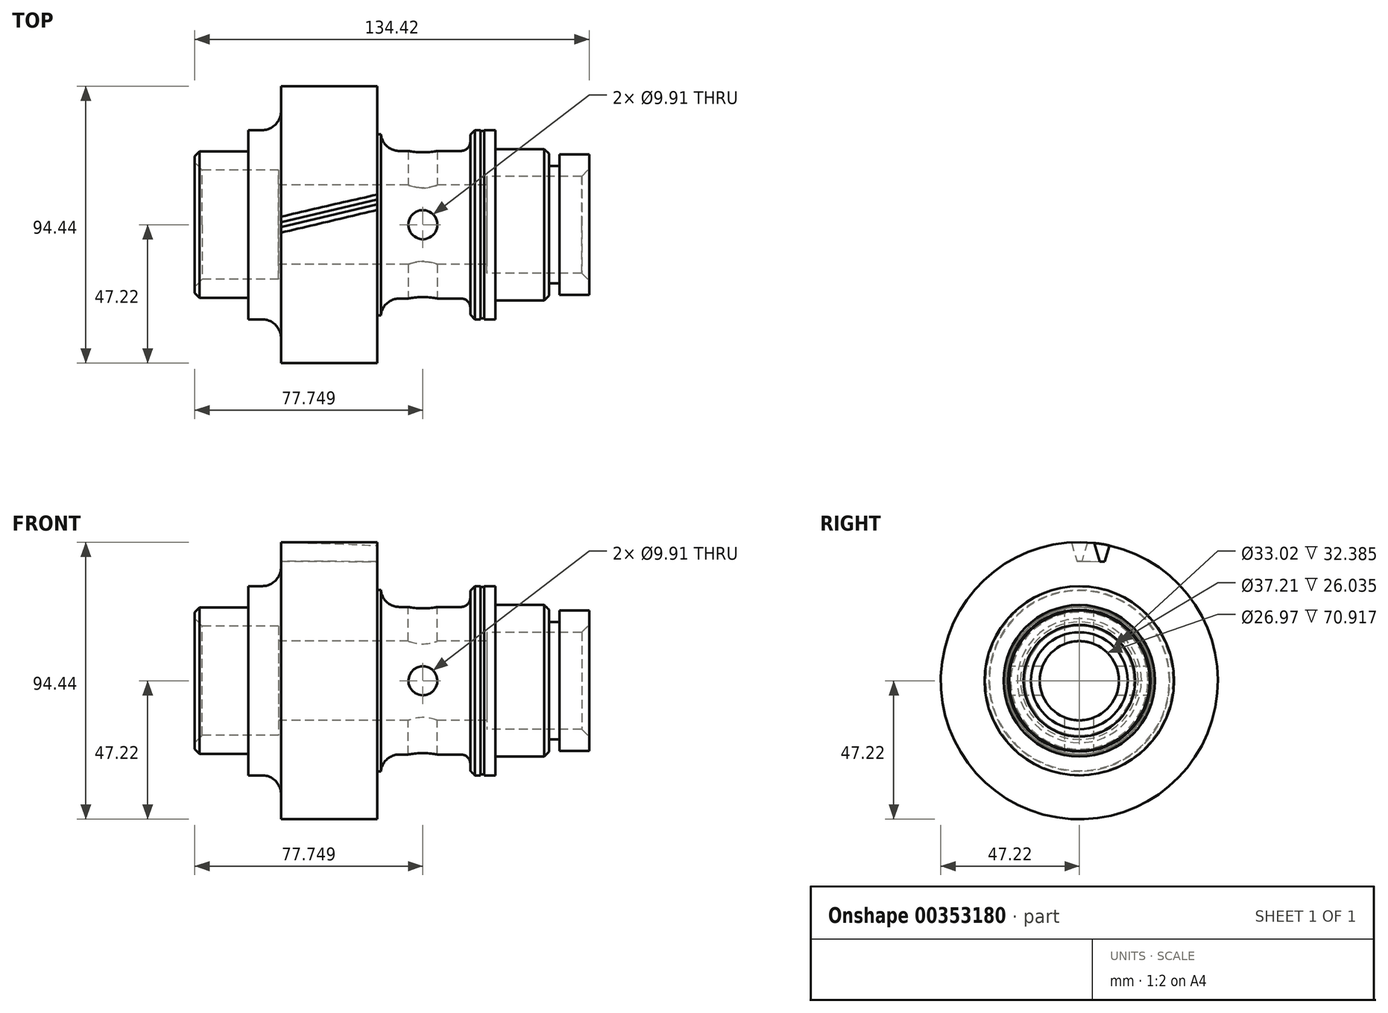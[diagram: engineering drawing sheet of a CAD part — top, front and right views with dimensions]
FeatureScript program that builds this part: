
annotation { "Feature Type Name" : "Feature", "Feature Type Description" : "" }
export const myFeature = defineFeature(function(context is Context, id is Id, definition is map)
    precondition{}
    {
        {
            var Q0;
            Q0=qCreatedBy(makeId("Front.planeOp"),FACE);
            var sketch = newSketch(context, id + "F0", { "sketchPlane" : qUnion([Q0])});
            skLineSegment(sketch, "E0", {"start": v(0, 0) * mm, "end": v(134.42, 0) * mm});
            skLineSegment(sketch, "E1", {"start": v(134.42, 0) * mm, "end": v(134.42, 23.94) * mm});
            skLineSegment(sketch, "E2", {"start": v(134.42, 23.94) * mm, "end": v(124.26, 23.94) * mm});
            skLineSegment(sketch, "E3", {"start": v(124.26, 23.94) * mm, "end": v(124.26, 20.02) * mm});
            skLineSegment(sketch, "E4", {"start": v(124.26, 20.02) * mm, "end": v(120.7, 20.02) * mm});
            skLineSegment(sketch, "E5", {"start": v(120.7, 20.02) * mm, "end": v(120.7, 25.8) * mm});
            skLineSegment(sketch, "E6", {"start": v(120.7, 25.8) * mm, "end": v(102.41, 25.8) * mm});
            skLineSegment(sketch, "E7", {"start": v(102.41, 25.8) * mm, "end": v(102.41, 32.26) * mm});
            skLineSegment(sketch, "E8", {"start": v(102.41, 32.26) * mm, "end": v(98.6, 32.26) * mm});
            skLineSegment(sketch, "E9", {"start": v(98.6, 32.26) * mm, "end": v(98.6, 31.94) * mm});
            skLineSegment(sketch, "E10", {"start": v(98.6, 31.94) * mm, "end": v(97.33, 31.94) * mm});
            skLineSegment(sketch, "E11", {"start": v(97.33, 31.94) * mm, "end": v(97.33, 32.26) * mm});
            skLineSegment(sketch, "E12", {"start": v(97.33, 32.26) * mm, "end": v(93.9, 32.26) * mm});
            skLineSegment(sketch, "E13", {"start": v(93.9, 32.26) * mm, "end": v(93.9, 25.15) * mm});
            skLineSegment(sketch, "E14", {"start": v(93.9, 25.15) * mm, "end": v(63.42, 25.15) * mm});
            skLineSegment(sketch, "E15", {"start": v(62.15, 47.22) * mm, "end": v(29.39, 47.22) * mm});
            skLineSegment(sketch, "E16", {"start": v(29.39, 47.22) * mm, "end": v(29.39, 32.26) * mm});
            skLineSegment(sketch, "E17", {"start": v(29.39, 32.26) * mm, "end": v(18.29, 32.26) * mm});
            skLineSegment(sketch, "E18", {"start": v(18.29, 24.92) * mm, "end": v(0, 24.92) * mm});
            skLineSegment(sketch, "E19", {"start": v(0, 24.92) * mm, "end": v(0, 0) * mm});
            skLineSegment(sketch, "E20", {"start": v(63.42, 25.15) * mm, "end": v(63.42, 30.87) * mm});
            skLineSegment(sketch, "E21", {"start": v(63.42, 30.87) * mm, "end": v(62.15, 30.87) * mm});
            skLineSegment(sketch, "E22", {"start": v(62.15, 30.87) * mm, "end": v(62.15, 47.22) * mm});
            skLineSegment(sketch, "E23", {"start": v(18.29, 24.92) * mm, "end": v(18.29, 32.26) * mm});
            skPoint(sketch, "E24.orphan", {"position": v(9.8, 32.26) * mm});
            skLineSegment(sketch, "E25", {"start": v(0, 18.6) * mm, "end": v(28.57, 18.6) * mm});
            skLineSegment(sketch, "E26", {"start": v(28.58, 18.6) * mm, "end": v(28.58, 13.49) * mm});
            skLineSegment(sketch, "E27", {"start": v(28.58, 13.49) * mm, "end": v(99.5, 13.49) * mm});
            skLineSegment(sketch, "E28", {"start": v(99.5, 13.49) * mm, "end": v(99.5, 16.51) * mm});
            skLineSegment(sketch, "E29", {"start": v(99.5, 16.51) * mm, "end": v(134.42, 16.51) * mm});
            skSolve(sketch);
        }
        {
            var Q0;
            {var subQ3=sQuery(id+"F0.wireOp",EDGE,"E2");Q0=makeQuery(id+"F0.imprint","IMPRINT",FACE,{"disambiguationData":[TD([[makeQuery(id+"F0.imprint","IMPRINT",EDGE,{"derivedFrom":subQ3}),1.0]])]});}
            var Q1;
            Q1=sQuery(id+"F0.wireOp",EDGE,"E0");
            revolve(context, id + "F1", {"entities" : qUnion([Q0]), "axis" : qUnion([Q1]), "revolveType" : RevolveType.FULL});
        }
        {
            var Q0;
            Q0=makeQuery(id+"F1.opRevolve","SWEPT_EDGE",EDGE,{"disambiguationData":[OSD([sQuery(id+"F0.wireOp",EDGE,"E14"),sQuery(id+"F0.wireOp",EDGE,"E20")])]});
            var Q1;
            Q1=makeQuery(id+"F1.opRevolve","SWEPT_EDGE",EDGE,{"disambiguationData":[OSD([sQuery(id+"F0.wireOp",EDGE,"E16"),sQuery(id+"F0.wireOp",EDGE,"E17")])]});
            fillet(context, id + "F2", {"entities" : qUnion([Q0, Q1]), "radius" : 6.35 * mm, "tangentPropagation" : true, "allowEdgeOverflow" : false});
        }
        {
            var Q0;
            Q0=makeQuery(id+"F1.opRevolve","SWEPT_EDGE",EDGE,{"disambiguationData":[OSD([sQuery(id+"F0.wireOp",EDGE,"E13"),sQuery(id+"F0.wireOp",EDGE,"E14")])]});
            fillet(context, id + "F3", {"entities" : qUnion([Q0]), "radius" : 3.17 * mm, "tangentPropagation" : true, "allowEdgeOverflow" : false});
        }
        {
            var Q0;
            Q0=makeQuery(id+"F1.opRevolve","SWEPT_EDGE",EDGE,{"disambiguationData":[OSD([sQuery(id+"F0.wireOp",EDGE,"E12"),sQuery(id+"F0.wireOp",EDGE,"E13")])]});
            var Q1;
            Q1=makeQuery(id+"F1.opRevolve","SWEPT_EDGE",EDGE,{"disambiguationData":[OSD([sQuery(id+"F0.wireOp",EDGE,"E5"),sQuery(id+"F0.wireOp",EDGE,"E6")])]});
            var Q2;
            Q2=makeQuery(id+"F1.opRevolve","SWEPT_EDGE",EDGE,{"disambiguationData":[OSD([sQuery(id+"F0.wireOp",EDGE,"E18"),sQuery(id+"F0.wireOp",EDGE,"E19")])]});
            chamfer(context, id + "F4", {"entities" : qUnion([Q0, Q1, Q2]), "width" : 1.57 * mm, "tangentPropagation" : true});
        }
        {
            var Q0;
            Q0=makeQuery(id+"F1.opRevolve","SWEPT_EDGE",EDGE,{"disambiguationData":[OSD([sQuery(id+"F0.wireOp",EDGE,"E19"),sQuery(id+"F0.wireOp",EDGE,"E25")])]});
            var Q1;
            Q1=makeQuery(id+"F1.opRevolve","SWEPT_EDGE",EDGE,{"disambiguationData":[OSD([sQuery(id+"F0.wireOp",EDGE,"E1"),sQuery(id+"F0.wireOp",EDGE,"E29")])]});
            chamfer(context, id + "F5", {"entities" : qUnion([Q0, Q1]), "width" : 2.54 * mm, "tangentPropagation" : true});
        }
        {
            var Q0;
            Q0=qCreatedBy(makeId("Top.planeOp"),FACE);
            var sketch = newSketch(context, id + "F6", { "sketchPlane" : qUnion([Q0])});
            skCircle(sketch, "E30", {"center": v(77.75, 0) * mm, "radius": 4.95 * mm});
            skSolve(sketch);
        }
        {
            var Q0;
            Q0=makeQuery(id+"F6.imprint","IMPRINT",FACE,{"disambiguationData":[TD([[makeQuery(id+"F6.imprint","IMPRINT",EDGE,{"derivedFrom":sQuery(id+"F6.wireOp",EDGE,"E30")}),1.0]])]});
            extrude(context, id + "F7", {"entities" : qUnion([Q0]), "operationType" : NewBodyOperationType.REMOVE, "endBound" : BoundingType.THROUGH_ALL, "oppositeDirection" : true, "depth" : 25.4 * mm, "hasSecondDirection" : true, "secondDirectionBound" : SecondDirectionBoundingType.THROUGH_ALL, "secondDirectionOppositeDirection" : false, "secondDirectionDepth" : 25.4 * mm});
        }
        {
            var Q0;
            Q0=qCreatedBy(makeId("Front.planeOp"),FACE);
            var sketch = newSketch(context, id + "F8", { "sketchPlane" : qUnion([Q0])});
            skCircle(sketch, "E31", {"center": v(77.75, 0) * mm, "radius": 4.95 * mm});
            skSolve(sketch);
        }
        {
            var Q0;
            Q0 = qSketchRegion(id + "F8", true);
            extrude(context, id + "F9", {"entities" : qUnion([Q0]), "operationType" : NewBodyOperationType.REMOVE, "endBound" : BoundingType.THROUGH_ALL, "oppositeDirection" : true, "depth" : 25.4 * mm, "hasSecondDirection" : true, "secondDirectionBound" : SecondDirectionBoundingType.THROUGH_ALL, "secondDirectionOppositeDirection" : false, "secondDirectionDepth" : 25.4 * mm});
        }
        {
            var Q0;
            Q0=makeQuery(id+"F1.opRevolve","SWEPT_FACE",FACE,{"disambiguationData":[OSD([sQuery(id+"F0.wireOp",EDGE,"E16")])]});
            var sketch = newSketch(context, id + "F10", { "sketchPlane" : qUnion([Q0])});
            skLineSegment(sketch, "E32", {"start": v(0, 0) * mm, "end": v(0, 55.57) * mm, "construction": true});
            skCircle(sketch, "E33", {"center": v(0, 0) * mm, "radius": 40.77 * mm});
            skLineSegment(sketch, "E34.0", {"start": v(0.83, 0) * mm, "end": v(0.83, 55.57) * mm, "construction": true});
            skLineSegment(sketch, "E35.0", {"start": v(2.73, 0) * mm, "end": v(2.73, 55.57) * mm, "construction": true});
            skLineSegment(sketch, "E36", {"start": v(3.26, 48.9) * mm, "end": v(0.83, 40.76) * mm});
            skLineSegment(sketch, "E37.MirrorCS", {"start": v(-3.26, 48.9) * mm, "end": v(-0.83, 40.76) * mm});
            skPoint(sketch, "E38", {"position": v(2.73, 47.14) * mm});
            skCircle(sketch, "E39", {"center": v(0, 0) * mm, "radius": 49.02 * mm});
            skPoint(sketch, "E40.orphan", {"position": v(-2.73, 47.14) * mm});
            skLineSegment(sketch, "E41", {"start": v(-0.83, 40.76) * mm, "end": v(0.83, 40.76) * mm});
            skSolve(sketch);
        }
        {
            var Q0;
            Q0=makeQuery(id+"F1.opRevolve","SWEPT_FACE",FACE,{"disambiguationData":[OSD([sQuery(id+"F0.wireOp",EDGE,"E22")])]});
            var sketch = newSketch(context, id + "F11", { "sketchPlane" : qUnion([Q0])});
            skLineSegment(sketch, "E42", {"start": v(0, 0) * mm, "end": v(0, 55.65) * mm});
            skLineSegment(sketch, "E43", {"start": v(0, 0) * mm, "end": v(9.23, 55.33) * mm, "construction": true});
            skLineSegment(sketch, "E44.0", {"start": v(-0.83, 0.14) * mm, "end": v(8.4, 55.47) * mm, "construction": true});
            skLineSegment(sketch, "E45.0", {"start": v(-2.7, 0.45) * mm, "end": v(6.53, 55.78) * mm, "construction": true});
            skCircle(sketch, "E46", {"center": v(0, 0) * mm, "radius": 40.7 * mm});
            skLineSegment(sketch, "E47", {"start": v(5.87, 40.28) * mm, "end": v(5.05, 46.95) * mm});
            skLineSegment(sketch, "E48.MirrorCS", {"start": v(7.53, 40) * mm, "end": v(10.46, 46.04) * mm});
            skLineSegment(sketch, "E49", {"start": v(5.87, 40.28) * mm, "end": v(7.53, 40) * mm});
            skSolve(sketch);
        }
        {
            var Q0;
            Q0=sQuery(id+"F10.wireOp",VERTEX,"E38");
            var Q1;
            Q1=sQuery(id+"F11.wireOp",VERTEX,"E47.end");
            var Q2;
            Q2=sQuery(id+"F10.wireOp",VERTEX,"E40.orphan");
            cPlane(context, id + "F12", {"entities" : qUnion([Q0, Q1, Q2]), "cplaneType" : CPlaneType.THREE_POINT, "offset" : 25.4 * mm, "width" : 152.4 * mm, "height" : 152.4 * mm});
        }
        {
            var Q0;
            Q0=qCreatedBy(id+"F12.planeOp",FACE);
            var sketch = newSketch(context, id + "F13", { "sketchPlane" : qUnion([Q0])});
            skPoint(sketch, "E50.0", {"position": v(29.11, 2.73) * mm});
            skPoint(sketch, "E51.0", {"position": v(61.88, -5.05) * mm});
            skLineSegment(sketch, "E52", {"start": v(29.11, 2.73) * mm, "end": v(61.88, -5.05) * mm});
            skSolve(sketch);
        }
        {
            var Q0;
            {var subQ0=sQuery(id+"F10.wireOp",EDGE,"E41");var subQ1=sQuery(id+"F10.wireOp",EDGE,"E36");var subQ2=sQuery(id+"F10.wireOp",EDGE,"E33");var subQ3=makeQuery(id+"F10.imprint","INTERSECT",VERTEX,{"derivedFrom":[subQ2,subQ1,subQ0]});Q0=makeQuery(id+"F10.imprint","IMPRINT",FACE,{"disambiguationData":[TD([[makeQuery(id+"F10.imprint","IMPRINT",EDGE,{"disambiguationData":[TD([[subQ3,-1.0]])],"derivedFrom":subQ2}),-1.0]])]});}
            var Q1;
            {var subQ0=sQuery(id+"F10.wireOp",EDGE,"E39");var subQ1=sQuery(id+"F10.wireOp",EDGE,"E36");var subQ2=makeQuery(id+"F10.imprint","INTERSECT",VERTEX,{"derivedFrom":[subQ1,subQ0]});Q1=makeQuery(id+"F10.imprint","IMPRINT",FACE,{"disambiguationData":[TD([[makeQuery(id+"F10.imprint","IMPRINT",EDGE,{"disambiguationData":[TD([[subQ2,-1.0]])],"derivedFrom":subQ0}),1.0]])]});}
            var Q2;
            Q2=sQuery(id+"F13.wireOp",EDGE,"E52");
            sweep(context, id + "F14", {"operationType" : NewBodyOperationType.REMOVE, "profiles" : qUnion([Q0, Q1]), "path" : qUnion([Q2])});
        }
    });
